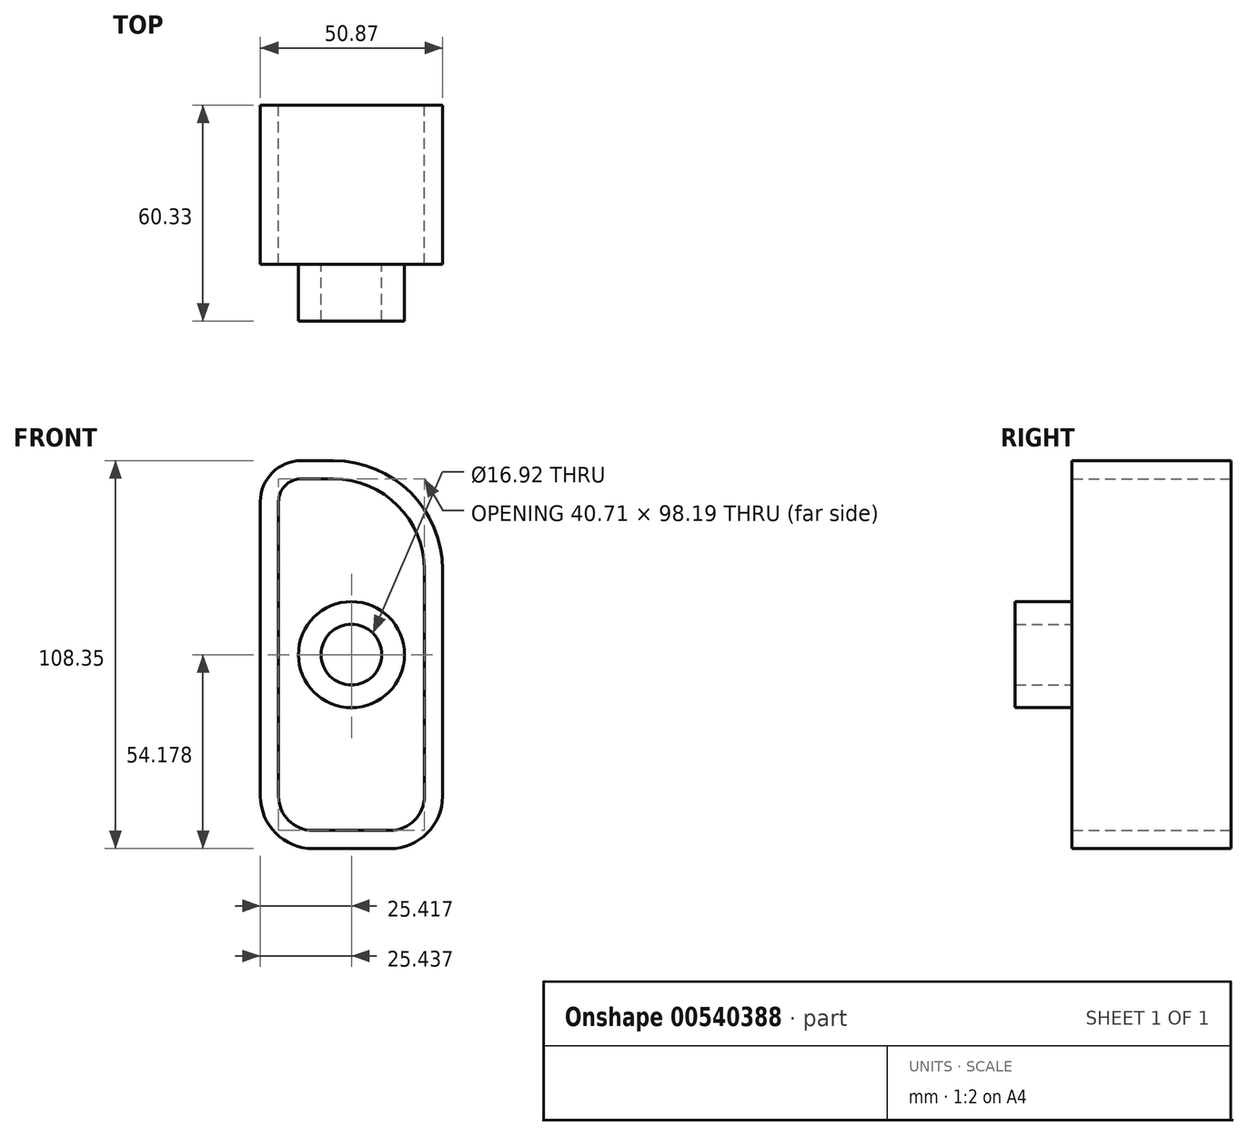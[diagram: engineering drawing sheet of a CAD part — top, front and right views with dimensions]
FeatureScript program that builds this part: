
annotation { "Feature Type Name" : "Feature", "Feature Type Description" : "" }
export const myFeature = defineFeature(function(context is Context, id is Id, definition is map)
    precondition{}
    {
        {
            var Q0;
            Q0=qCreatedBy(makeId("Front.planeOp"),FACE);
            var sketch = newSketch(context, id + "F0", { "sketchPlane" : qUnion([Q0])});
            skLineSegment(sketch, "E0.bottom", {"start": v(168.04, -11.84) * mm, "end": v(146.38, -11.84) * mm});
            skLineSegment(sketch, "E0.top", {"start": v(152.16, 86.35) * mm, "end": v(143.2, 86.35) * mm});
            skLineSegment(sketch, "E0.left", {"start": v(177.56, -2.31) * mm, "end": v(177.56, 60.95) * mm});
            skLineSegment(sketch, "E0.right", {"start": v(136.85, -2.31) * mm, "end": v(136.85, 80) * mm});
            skPoint(sketch, "E0.middle", {"position": v(157.2, 37.26) * mm});
            skCircle(sketch, "E1", {"center": v(157.2, 37.26) * mm, "radius": 8.46 * mm});
            skPoint(sketch, "E2.visualSharp", {"position": v(136.85, 86.35) * mm});
            skArc(sketch, "E2.filletArc", {"start": v(143.2, 86.35) * mm, "mid": v(138.71, 84.5) * mm, "end": v(136.85, 80) * mm});
            skPoint(sketch, "E3.visualSharp", {"position": v(177.56, 86.35) * mm});
            skArc(sketch, "E3.filletArc", {"start": v(177.56, 60.95) * mm, "mid": v(170.12, 78.91) * mm, "end": v(152.16, 86.35) * mm});
            skPoint(sketch, "E4.visualSharp", {"position": v(136.85, -11.84) * mm});
            skArc(sketch, "E4.filletArc", {"start": v(136.85, -2.31) * mm, "mid": v(139.64, -9.05) * mm, "end": v(146.38, -11.84) * mm});
            skPoint(sketch, "E5.visualSharp", {"position": v(177.56, -11.84) * mm});
            skArc(sketch, "E5.filletArc", {"start": v(168.04, -11.84) * mm, "mid": v(174.77, -9.05) * mm, "end": v(177.56, -2.31) * mm});
            skArc(sketch, "E6.0", {"start": v(131.77, -2.31) * mm, "mid": v(136.05, -12.64) * mm, "end": v(146.38, -16.92) * mm});
            skLineSegment(sketch, "E6.1", {"start": v(168.04, -16.92) * mm, "end": v(146.38, -16.92) * mm});
            skLineSegment(sketch, "E6.2", {"start": v(131.77, -2.31) * mm, "end": v(131.77, 80) * mm});
            skArc(sketch, "E6.3", {"start": v(168.04, -16.92) * mm, "mid": v(178.37, -12.64) * mm, "end": v(182.64, -2.31) * mm});
            skArc(sketch, "E6.4", {"start": v(143.2, 91.43) * mm, "mid": v(135.12, 88.09) * mm, "end": v(131.77, 80) * mm});
            skLineSegment(sketch, "E6.5", {"start": v(152.16, 91.43) * mm, "end": v(143.2, 91.43) * mm});
            skArc(sketch, "E6.6", {"start": v(182.64, 60.95) * mm, "mid": v(173.72, 82.5) * mm, "end": v(152.16, 91.43) * mm});
            skLineSegment(sketch, "E6.7", {"start": v(182.64, -2.31) * mm, "end": v(182.64, 60.95) * mm});
            skSolve(sketch);
        }
        {
            var Q0;
            Q0 = qSketchRegion(id + "F0", true);
            extrude(context, id + "F1", {"entities" : qUnion([Q0]), "depth" : 44.45 * mm, "offsetDistance" : 25.4 * mm});
        }
        {
            var Q0;
            Q0=makeQuery(id+"F1.opExtrude","CAP_FACE",FACE,{"disambiguationData":[OSD([sQuery(id+"F0.wireOp",EDGE,"E0.bottom"),sQuery(id+"F0.wireOp",EDGE,"E0.top"),sQuery(id+"F0.wireOp",EDGE,"E0.left"),sQuery(id+"F0.wireOp",EDGE,"E0.right"),sQuery(id+"F0.wireOp",EDGE,"E1")])],"isStart":false});
            var sketch = newSketch(context, id + "F2", { "sketchPlane" : qUnion([Q0])});
            skCircle(sketch, "E7.0", {"center": v(157.19, 37.26) * mm, "radius": 8.46 * mm});
            skCircle(sketch, "E8.0", {"center": v(157.19, 37.26) * mm, "radius": 14.8 * mm});
            skSolve(sketch);
        }
        {
            var Q0;
            Q0 = qSketchRegion(id + "F2", true);
            extrude(context, id + "F3", {"entities" : qUnion([Q0]), "operationType" : NewBodyOperationType.ADD, "depth" : 15.88 * mm, "offsetDistance" : 25.4 * mm});
        }
    });
